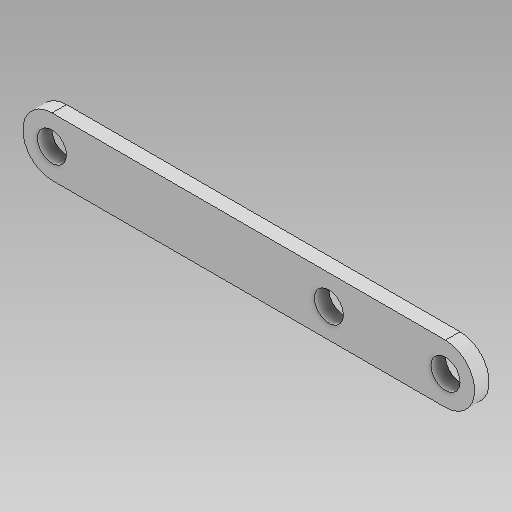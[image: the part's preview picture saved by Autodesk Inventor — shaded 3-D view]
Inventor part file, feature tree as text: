
AUTODESK INVENTOR PART (.ipt)
format: ipt  version: 2025 (Build 290162000, 162)  size: 97,280 bytes
history: native  units: in
note: dims shown in document units (in); Inventor stores cm internally (conversion verified against a paired STEP export)
features: other x1, extrude x1, sketch x1
ambient origin geometry x8: Origin, YZ Plane, XZ Plane, XY Plane, X Axis, Y Axis, Z Axis, Center Point
bodies: Body1 (feature_tree)
feature tree (3):
  other  "솔리드1"
  extrude  "돌출1"  Depth=0.7874in
  sketch  "스케치1"
